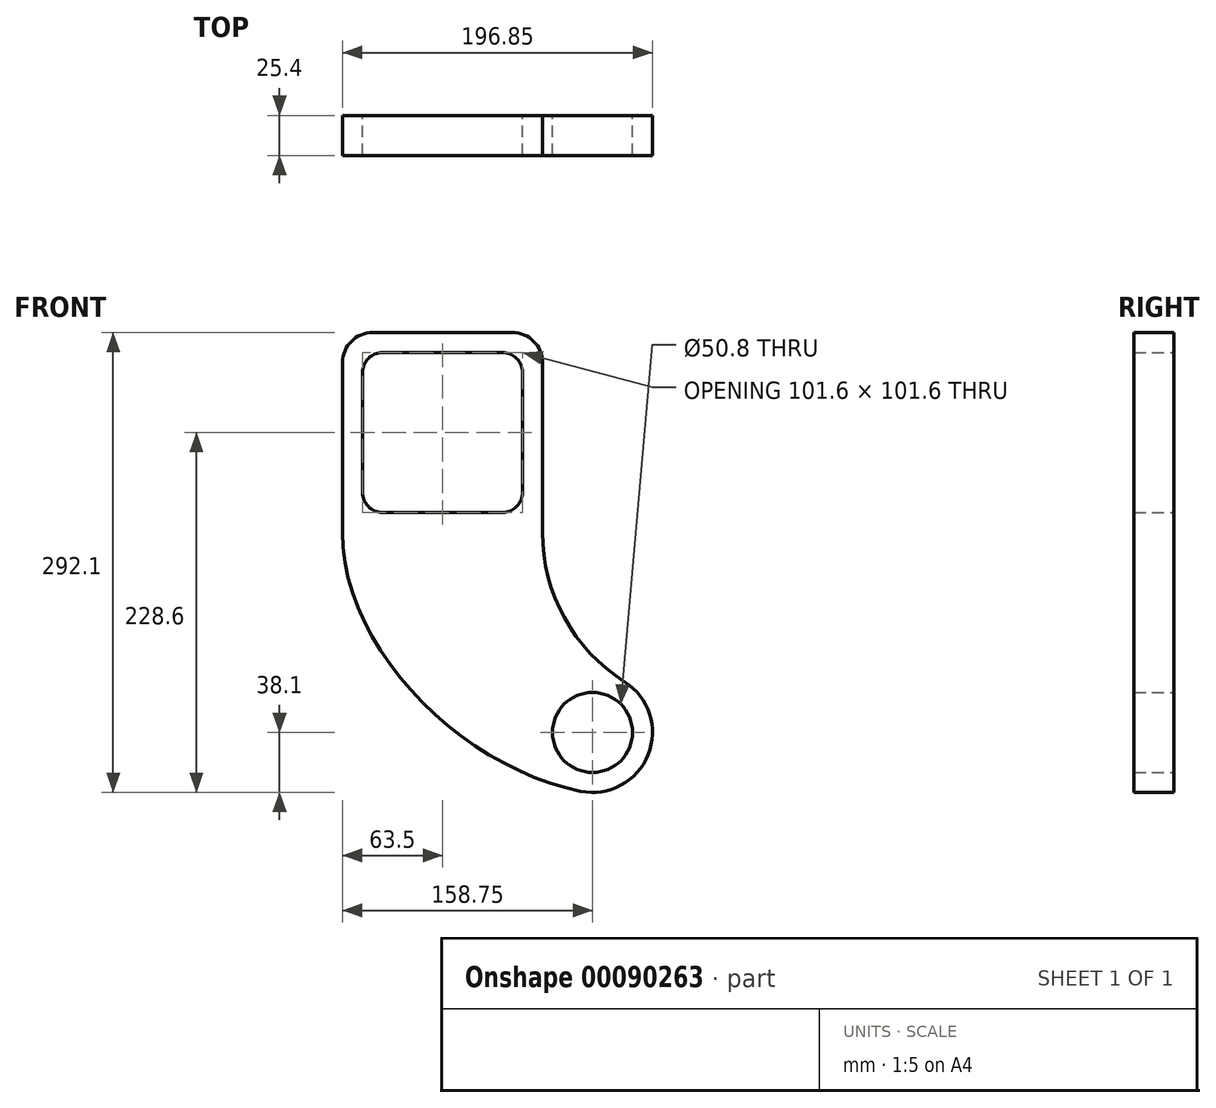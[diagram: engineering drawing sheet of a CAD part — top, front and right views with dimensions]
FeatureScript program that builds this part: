
annotation { "Feature Type Name" : "Feature", "Feature Type Description" : "" }
export const myFeature = defineFeature(function(context is Context, id is Id, definition is map)
    precondition{}
    {
        {
            var Q0;
            Q0=qCreatedBy(makeId("Front.planeOp"),FACE);
            var sketch = newSketch(context, id + "F0", { "sketchPlane" : qUnion([Q0])});
            skLineSegment(sketch, "E0", {"start": v(19.05, 0) * mm, "end": v(107.95, 0) * mm});
            skLineSegment(sketch, "E1", {"start": v(127, -19.05) * mm, "end": v(127, -127) * mm});
            skArc(sketch, "E2", {"start": v(127, -127) * mm, "mid": v(140.9, -181.1) * mm, "end": v(179.15, -221.82) * mm});
            skLineSegment(sketch, "E3", {"start": v(0, -19.05) * mm, "end": v(0, -127) * mm});
            skArc(sketch, "E4", {"start": v(151.28, -291.36) * mm, "mid": v(194.11, -268.18) * mm, "end": v(179.15, -221.82) * mm});
            skCircle(sketch, "E5", {"center": v(158.75, -254) * mm, "radius": 25.4 * mm});
            skPoint(sketch, "E6.visualSharp", {"position": v(0, 0) * mm});
            skArc(sketch, "E6.filletArc", {"start": v(19.05, 0) * mm, "mid": v(5.58, -5.58) * mm, "end": v(0, -19.05) * mm});
            skPoint(sketch, "E7.visualSharp", {"position": v(127, 0) * mm});
            skArc(sketch, "E7.filletArc", {"start": v(127, -19.05) * mm, "mid": v(121.42, -5.58) * mm, "end": v(107.95, 0) * mm});
            skPoint(sketch, "E8.visualSharp", {"position": v(0, -127) * mm});
            skLineSegment(sketch, "E9", {"start": v(63.5, 0) * mm, "end": v(63.5, -127) * mm, "construction": true});
            skLineSegment(sketch, "E10.top", {"start": v(25.4, -114.3) * mm, "end": v(101.6, -114.3) * mm});
            skLineSegment(sketch, "E10.left", {"start": v(12.7, -25.4) * mm, "end": v(12.7, -101.6) * mm});
            skLineSegment(sketch, "E10.right", {"start": v(114.3, -25.4) * mm, "end": v(114.3, -101.6) * mm});
            skPoint(sketch, "E11", {"position": v(63.5, -114.3) * mm});
            skPoint(sketch, "E12.visualSharp", {"position": v(12.7, -114.3) * mm});
            skArc(sketch, "E12.filletArc", {"start": v(12.7, -101.6) * mm, "mid": v(16.42, -110.58) * mm, "end": v(25.4, -114.3) * mm});
            skPoint(sketch, "E13.visualSharp", {"position": v(114.3, -114.3) * mm});
            skArc(sketch, "E13.filletArc", {"start": v(101.6, -114.3) * mm, "mid": v(110.58, -110.58) * mm, "end": v(114.3, -101.6) * mm});
            skLineSegment(sketch, "E14", {"start": v(25.4, -12.7) * mm, "end": v(101.6, -12.7) * mm});
            skPoint(sketch, "E15.visualSharp", {"position": v(12.7, -12.7) * mm});
            skArc(sketch, "E15.filletArc", {"start": v(25.4, -12.7) * mm, "mid": v(16.42, -16.42) * mm, "end": v(12.7, -25.4) * mm});
            skPoint(sketch, "E16.visualSharp", {"position": v(114.3, -12.7) * mm});
            skArc(sketch, "E16.filletArc", {"start": v(114.3, -25.4) * mm, "mid": v(110.58, -16.42) * mm, "end": v(101.6, -12.7) * mm});
            skFitSpline(sketch, "E17", {"points": [v(0, -127) * mm, v(151.28, -291.36) * mm], "startDerivative": vector(0, -220.98) * mm, "endDerivative": vector(228.6, -45.72) * mm});
            skSolve(sketch);
        }
        {
            var Q0;
            Q0=makeQuery(id+"F0.imprint","IMPRINT",FACE,{"disambiguationData":[TD([[makeQuery(id+"F0.imprint","IMPRINT",EDGE,{"derivedFrom":sQuery(id+"F0.wireOp",EDGE,"E0")}),-1.0]])]});
            extrude(context, id + "F1", {"entities" : qUnion([Q0]), "depth" : 25.4 * mm});
        }
    });
